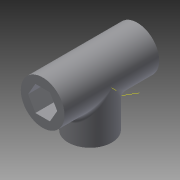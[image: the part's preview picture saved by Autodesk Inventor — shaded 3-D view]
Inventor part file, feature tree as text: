
AUTODESK INVENTOR PART (.ipt)
format: ipt  version: 2015 SP1 (Build 190203100, 203)  size: 213,504 bytes
history: native  units: mm
features: other x4, extrude x4, sketch x4, pattern_circular x2, projected_geometry x2, fillet x1
ambient origin geometry x8: Origin, YZ Plane, XZ Plane, XY Plane, X Axis, Y Axis, Z Axis, Center Point
bodies: Body1 (feature_tree)
feature tree (17):
  other  "Sólido1"
  extrude  "Extrusión1"  Depth=12.0mm
  extrude  "Extrusión2"  Depth=6.0mm TaperAngle=0.0deg
  other  "Eje de trabajo1"
  other  "Eje de trabajo2"
  pattern_circular  "Patrón circular3"  Count=2 Angle=90.0deg
  pattern_circular  "Patrón circular4"  Count=2  [1 undecoded]
  extrude  "Extrusión11"  Depth=10.0mm TaperAngle=0.0deg
  extrude  "Extrusión12"  [1 undecoded]
  fillet  "Empalme4"  [1 undecoded]
  sketch  "Boceto1"  dims[d0=8.0mm d1=12.0mm]
  sketch  "Boceto2"  dims[d2=7.0mm d3=0.0mm d4=6.0mm d5=0.0mm d19=20.0mm d20=90.0deg d34=20.0mm d35=-15.707963mm]
  other  "Punto de trabajo1"
  sketch  "Boceto12"  dims[d37=200.0mm d38=0.0mm d39=10.0mm d40=0.0mm]
  projected_geometry  "Contorno proyectado10"
  sketch  "Boceto13"  dims[d41=2.0mm]
  projected_geometry  "Contorno proyectado11"
note: 3 required parameter values undecoded (feature->parameter linkage not recoverable at this tier; creation-order binding heuristic only, values carry confidence <= 0.55)
